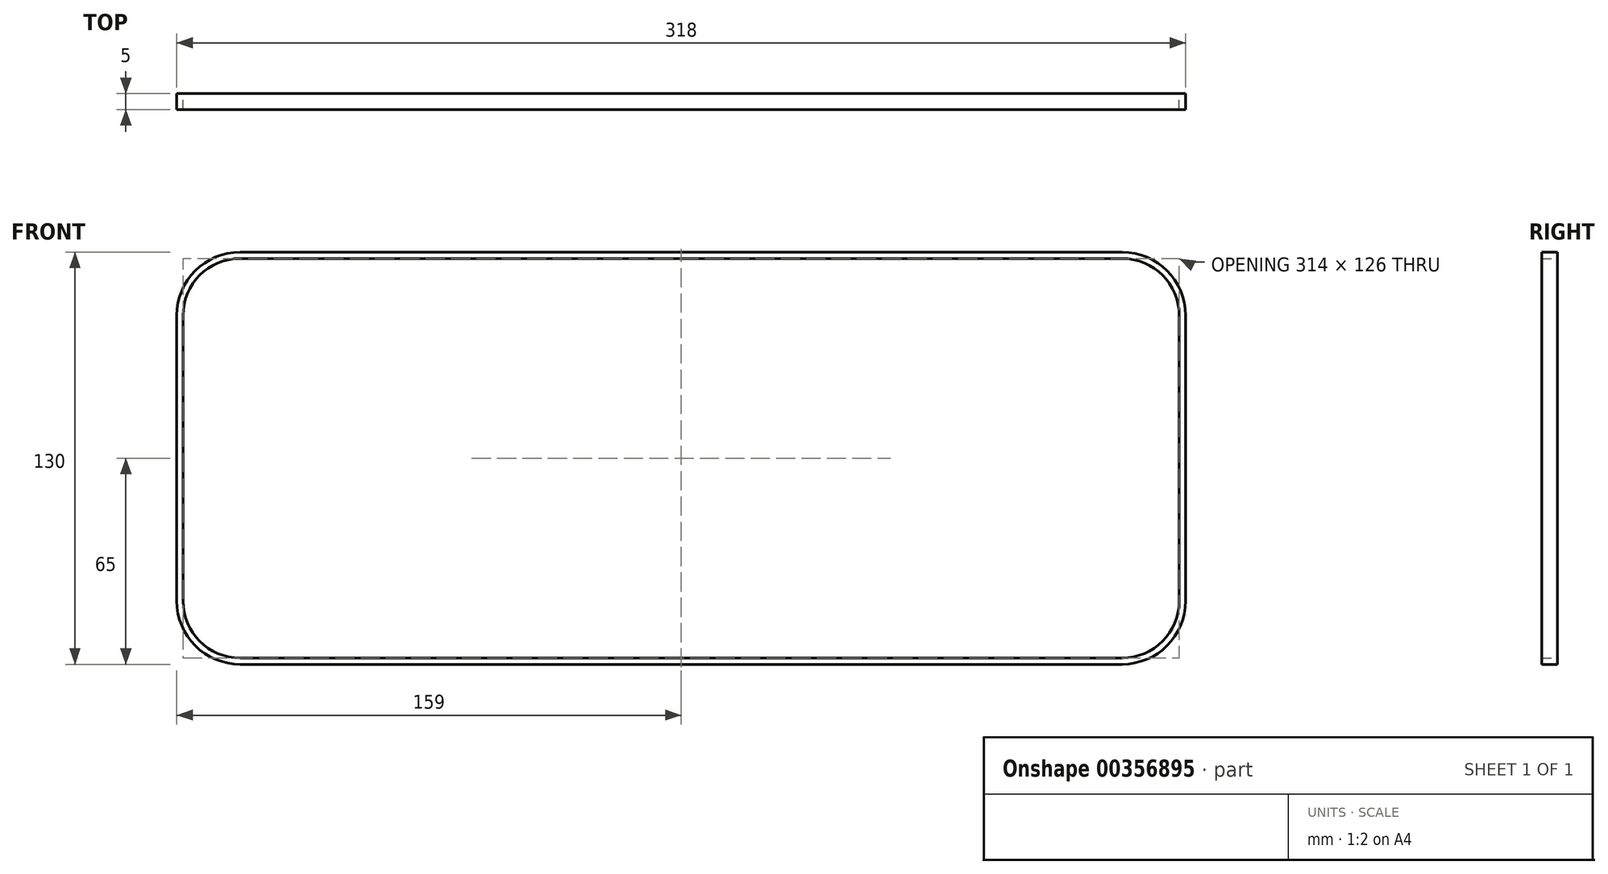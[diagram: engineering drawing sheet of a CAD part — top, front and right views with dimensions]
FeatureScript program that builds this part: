
annotation { "Feature Type Name" : "Feature", "Feature Type Description" : "" }
export const myFeature = defineFeature(function(context is Context, id is Id, definition is map)
    precondition{}
    {
        {
            var Q0;
            Q0=qCreatedBy(makeId("Front.planeOp"),FACE);
            var sketch = newSketch(context, id + "F0", { "sketchPlane" : qUnion([Q0])});
            skLineSegment(sketch, "E0.bottom", {"start": v(159, 65) * mm, "end": v(-159, 65) * mm});
            skLineSegment(sketch, "E0.top", {"start": v(159, -65) * mm, "end": v(-159, -65) * mm});
            skLineSegment(sketch, "E0.left", {"start": v(159, 65) * mm, "end": v(159, -65) * mm});
            skLineSegment(sketch, "E0.right", {"start": v(-159, 65) * mm, "end": v(-159, -65) * mm});
            skPoint(sketch, "E0.middle", {"position": v(0, 0) * mm});
            skSolve(sketch);
        }
        {
            var Q0;
            Q0=makeQuery(id+"F0.imprint","IMPRINT",FACE,{"disambiguationData":[TD([[makeQuery(id+"F0.imprint","IMPRINT",EDGE,{"derivedFrom":sQuery(id+"F0.wireOp",EDGE,"E0.bottom")}),1.0]])]});
            extrude(context, id + "F1", {"entities" : qUnion([Q0]), "depth" : 5 * mm});
        }
        {
            var Q0;
            Q0=makeQuery(id+"F1.opExtrude","SWEPT_EDGE",EDGE,{"disambiguationData":[OSD([sQuery(id+"F0.wireOp",EDGE,"E0.top"),sQuery(id+"F0.wireOp",EDGE,"E0.right")])]});
            var Q1;
            Q1=makeQuery(id+"F1.opExtrude","SWEPT_EDGE",EDGE,{"disambiguationData":[OSD([sQuery(id+"F0.wireOp",EDGE,"E0.top"),sQuery(id+"F0.wireOp",EDGE,"E0.left")])]});
            var Q2;
            Q2=makeQuery(id+"F1.opExtrude","SWEPT_EDGE",EDGE,{"disambiguationData":[OSD([sQuery(id+"F0.wireOp",EDGE,"E0.bottom"),sQuery(id+"F0.wireOp",EDGE,"E0.left")])]});
            var Q3;
            Q3=makeQuery(id+"F1.opExtrude","SWEPT_EDGE",EDGE,{"disambiguationData":[OSD([sQuery(id+"F0.wireOp",EDGE,"E0.bottom"),sQuery(id+"F0.wireOp",EDGE,"E0.right")])]});
            fillet(context, id + "F2", {"entities" : qUnion([Q0, Q1, Q2, Q3]), "radius" : 20 * mm, "tangentPropagation" : true, "allowEdgeOverflow" : false});
        }
        {
            var Q0;
            Q0=makeQuery(id+"F1.opExtrude","CAP_FACE",FACE,{"disambiguationData":[OSD([sQuery(id+"F0.wireOp",EDGE,"E0.bottom"),sQuery(id+"F0.wireOp",EDGE,"E0.top"),sQuery(id+"F0.wireOp",EDGE,"E0.left"),sQuery(id+"F0.wireOp",EDGE,"E0.right")])],"isStart":false});
            var Q1;
            Q1=makeQuery(id+"F1.opExtrude","CAP_FACE",FACE,{"disambiguationData":[OSD([sQuery(id+"F0.wireOp",EDGE,"E0.bottom"),sQuery(id+"F0.wireOp",EDGE,"E0.top"),sQuery(id+"F0.wireOp",EDGE,"E0.left"),sQuery(id+"F0.wireOp",EDGE,"E0.right")])],"isStart":true});
            shell(context, id + "F3", {"entities" : qUnion([Q0, Q1]), "thickness" : 2 * mm});
        }
    });
